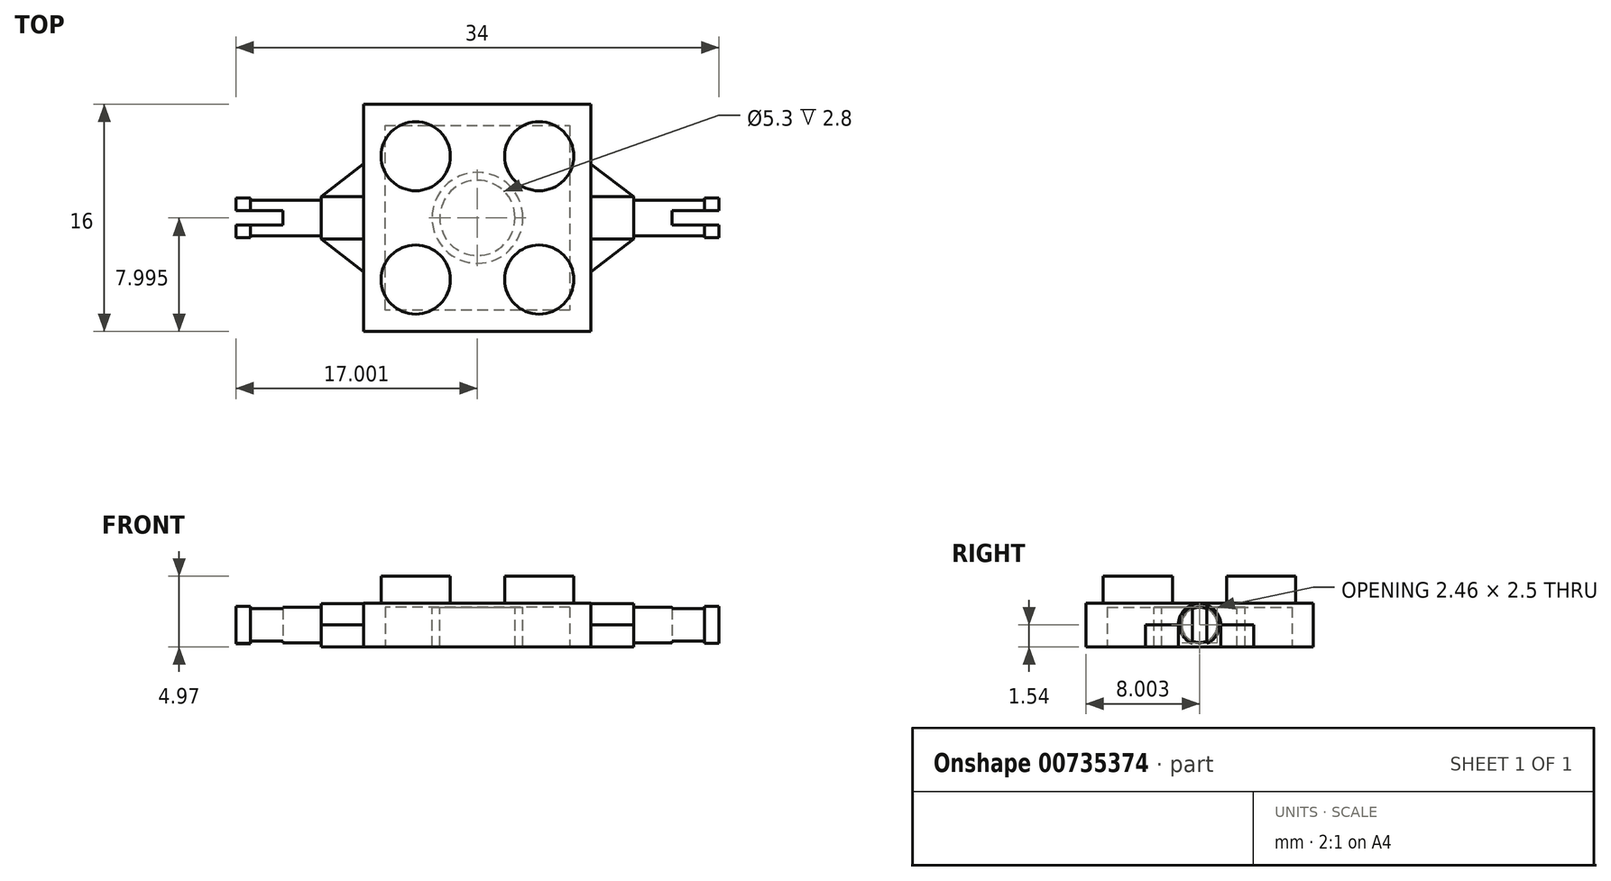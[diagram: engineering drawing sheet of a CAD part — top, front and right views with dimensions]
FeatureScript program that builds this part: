
annotation { "Feature Type Name" : "Feature", "Feature Type Description" : "" }
export const myFeature = defineFeature(function(context is Context, id is Id, definition is map)
    precondition{}
    {
        {
            var Q0;
            Q0=qCreatedBy(makeId("Top.planeOp"),FACE);
            var sketch = newSketch(context, id + "F0", { "sketchPlane" : qUnion([Q0])});
            skLineSegment(sketch, "E0", {"start": v(-18.34, 23.52) * mm, "end": v(-2.34, 23.52) * mm});
            skLineSegment(sketch, "E1", {"start": v(-18.34, 23.52) * mm, "end": v(-18.34, 7.52) * mm});
            skLineSegment(sketch, "E2", {"start": v(-18.34, 7.52) * mm, "end": v(-2.34, 7.52) * mm});
            skLineSegment(sketch, "E3", {"start": v(-2.34, 23.52) * mm, "end": v(-2.34, 7.52) * mm});
            skSolve(sketch);
        }
        {
            var Q0;
            Q0 = qSketchRegion(id + "F0", true);
            extrude(context, id + "F1", {"entities" : qUnion([Q0]), "depth" : 3.08 * mm, "offsetDistance" : 25 * mm});
        }
        {
            var Q0;
            Q0=makeQuery(id+"F1.opExtrude","CAP_FACE",FACE,{"disambiguationData":[OSD([sQuery(id+"F0.wireOp",EDGE,"E0"),sQuery(id+"F0.wireOp",EDGE,"E1"),sQuery(id+"F0.wireOp",EDGE,"E2"),sQuery(id+"F0.wireOp",EDGE,"E3")])],"isStart":false});
            var sketch = newSketch(context, id + "F2", { "sketchPlane" : qUnion([Q0])});
            skCircle(sketch, "E4", {"center": v(-14.68, 19.86) * mm, "radius": 2.44 * mm});
            skCircle(sketch, "E5", {"center": v(-6, 19.86) * mm, "radius": 2.44 * mm});
            skCircle(sketch, "E6", {"center": v(-14.68, 11.17) * mm, "radius": 2.44 * mm});
            skCircle(sketch, "E7", {"center": v(-6, 11.17) * mm, "radius": 2.44 * mm});
            skSolve(sketch);
        }
        {
            var Q0;
            Q0 = qSketchRegion(id + "F2", true);
            extrude(context, id + "F3", {"entities" : qUnion([Q0]), "operationType" : NewBodyOperationType.ADD, "depth" : 1.89 * mm, "offsetDistance" : 25 * mm});
        }
        {
            var Q0;
            Q0=makeQuery(id+"F1.opExtrude","SWEPT_FACE",FACE,{"disambiguationData":[OSD([sQuery(id+"F0.wireOp",EDGE,"E3")])]});
            var sketch = newSketch(context, id + "F4", { "sketchPlane" : qUnion([Q0])});
            skCircle(sketch, "E8", {"center": v(15.52, 1.54) * mm, "radius": 1.5 * mm});
            skPoint(sketch, "E8.centerSnap0", {"position": v(23.52, 1.54) * mm});
            skPoint(sketch, "E8.centerSnap1", {"position": v(15.52, 3.08) * mm});
            skSolve(sketch);
        }
        {
            var Q0;
            Q0 = qSketchRegion(id + "F4", true);
            extrude(context, id + "F5", {"entities" : qUnion([Q0]), "operationType" : NewBodyOperationType.ADD, "depth" : 3 * mm, "offsetDistance" : 25 * mm});
        }
        {
            var Q0;
            Q0=makeQuery(id+"F1.opExtrude","SWEPT_FACE",FACE,{"disambiguationData":[OSD([sQuery(id+"F0.wireOp",EDGE,"E1")])]});
            var sketch = newSketch(context, id + "F6", { "sketchPlane" : qUnion([Q0])});
            skCircle(sketch, "E9", {"center": v(-15.52, 1.54) * mm, "radius": 1.5 * mm});
            skPoint(sketch, "E9.centerSnap0", {"position": v(-7.52, 1.54) * mm});
            skPoint(sketch, "E9.centerSnap1", {"position": v(-15.52, 3.08) * mm});
            skSolve(sketch);
        }
        {
            var Q0;
            Q0 = qSketchRegion(id + "F6", true);
            extrude(context, id + "F7", {"entities" : qUnion([Q0]), "operationType" : NewBodyOperationType.ADD, "depth" : 3 * mm, "offsetDistance" : 25 * mm});
        }
        {
            var Q0;
            Q0=makeQuery(id+"F7.opExtrude","CAP_FACE",FACE,{"disambiguationData":[OSD([sQuery(id+"F6.wireOp",EDGE,"E9")])],"isStart":false});
            var sketch = newSketch(context, id + "F8", { "sketchPlane" : qUnion([Q0])});
            skCircle(sketch, "E10", {"center": v(-15.52, 1.54) * mm, "radius": 1.25 * mm});
            skSolve(sketch);
        }
        {
            var Q0;
            Q0 = qSketchRegion(id + "F8", true);
            extrude(context, id + "F9", {"entities" : qUnion([Q0]), "operationType" : NewBodyOperationType.ADD, "depth" : 5 * mm, "offsetDistance" : 25 * mm});
        }
        {
            var Q0;
            Q0=makeQuery(id+"F5.opExtrude","CAP_FACE",FACE,{"disambiguationData":[OSD([sQuery(id+"F4.wireOp",EDGE,"E8")])],"isStart":false});
            var sketch = newSketch(context, id + "F10", { "sketchPlane" : qUnion([Q0])});
            skCircle(sketch, "E11", {"center": v(15.52, 1.54) * mm, "radius": 1.25 * mm});
            skSolve(sketch);
        }
        {
            var Q0;
            Q0 = qSketchRegion(id + "F10", true);
            extrude(context, id + "F11", {"entities" : qUnion([Q0]), "operationType" : NewBodyOperationType.ADD, "depth" : 5 * mm, "offsetDistance" : 25 * mm});
        }
        {
            var Q0;
            Q0=makeQuery(id+"F1.opExtrude","SWEPT_FACE",FACE,{"disambiguationData":[OSD([sQuery(id+"F0.wireOp",EDGE,"E1")])]});
            var sketch = newSketch(context, id + "F12", { "sketchPlane" : qUnion([Q0])});
            skLineSegment(sketch, "E12", {"start": v(-19.32, 1.54) * mm, "end": v(-19.32, 0) * mm});
            skPoint(sketch, "E12.startSnap0", {"position": v(-23.52, 1.54) * mm});
            skLineSegment(sketch, "E13", {"start": v(-19.32, 0) * mm, "end": v(-11.72, 0) * mm});
            skLineSegment(sketch, "E14", {"start": v(-11.72, 0) * mm, "end": v(-11.72, 1.54) * mm});
            skLineSegment(sketch, "E15", {"start": v(-11.72, 1.54) * mm, "end": v(-14.02, 1.54) * mm});
            skLineSegment(sketch, "E16", {"start": v(-19.32, 1.54) * mm, "end": v(-17.02, 1.54) * mm});
            skSolve(sketch);
        }
        {
            var Q0;
            Q0 = qSketchRegion(id + "F12", true);
            var Q1;
            Q1=makeQuery(id+"F12.imprint","IMPRINT",FACE,{"disambiguationData":[TD([[makeQuery(id+"F12.imprint","IMPRINT",EDGE,{"derivedFrom":sQuery(id+"F12.wireOp",EDGE,"E12")}),1.0]])]});
            extrude(context, id + "F13", {"entities" : qUnion([Q0, Q1]), "operationType" : NewBodyOperationType.ADD, "depth" : 3 * mm, "offsetDistance" : 25 * mm});
        }
        {
            var Q0;
            Q0=makeQuery(id+"F1.opExtrude","SWEPT_FACE",FACE,{"disambiguationData":[OSD([sQuery(id+"F0.wireOp",EDGE,"E3")])]});
            var sketch = newSketch(context, id + "F14", { "sketchPlane" : qUnion([Q0])});
            skLineSegment(sketch, "E17", {"start": v(11.72, 1.54) * mm, "end": v(11.72, 0) * mm});
            skPoint(sketch, "E17.startSnap0", {"position": v(7.52, 1.54) * mm});
            skLineSegment(sketch, "E18", {"start": v(11.72, 0) * mm, "end": v(19.32, 0) * mm});
            skLineSegment(sketch, "E19", {"start": v(19.32, 0) * mm, "end": v(19.32, 1.54) * mm});
            skLineSegment(sketch, "E20", {"start": v(19.32, 1.54) * mm, "end": v(17.02, 1.54) * mm});
            skLineSegment(sketch, "E21", {"start": v(11.72, 1.54) * mm, "end": v(14.02, 1.54) * mm});
            skSolve(sketch);
        }
        {
            var Q0;
            Q0 = qSketchRegion(id + "F14", true);
            var Q1;
            Q1=makeQuery(id+"F14.imprint","IMPRINT",FACE,{"disambiguationData":[TD([[makeQuery(id+"F14.imprint","IMPRINT",EDGE,{"derivedFrom":sQuery(id+"F14.wireOp",EDGE,"E17")}),1.0]])]});
            extrude(context, id + "F15", {"entities" : qUnion([Q0, Q1]), "operationType" : NewBodyOperationType.ADD, "depth" : 3 * mm, "offsetDistance" : 25 * mm});
        }
        {
            var Q0;
            Q0=makeQuery(id+"F13.opExtrude","SWEPT_FACE",FACE,{"disambiguationData":[OSD([sQuery(id+"F12.wireOp",EDGE,"E16")])]});
            var sketch = newSketch(context, id + "F16", { "sketchPlane" : qUnion([Q0])});
            skLineSegment(sketch, "E22", {"start": v(-18.34, 19.32) * mm, "end": v(-21.34, 19.32) * mm});
            skLineSegment(sketch, "E23", {"start": v(-21.34, 19.32) * mm, "end": v(-21.34, 17.02) * mm});
            skLineSegment(sketch, "E24", {"start": v(-21.34, 17.02) * mm, "end": v(-18.34, 19.32) * mm});
            skLineSegment(sketch, "E25", {"start": v(-21.34, 11.72) * mm, "end": v(-21.34, 14.02) * mm});
            skLineSegment(sketch, "E26", {"start": v(-21.34, 14.02) * mm, "end": v(-18.34, 11.72) * mm});
            skLineSegment(sketch, "E27", {"start": v(-18.34, 11.72) * mm, "end": v(-21.34, 11.72) * mm});
            skSolve(sketch);
        }
        {
            var Q0;
            Q0=makeQuery(id+"F16.imprint","IMPRINT",FACE,{"disambiguationData":[TD([[makeQuery(id+"F16.imprint","IMPRINT",EDGE,{"derivedFrom":sQuery(id+"F16.wireOp",EDGE,"E25")}),-1.0]])]});
            var Q1;
            Q1=makeQuery(id+"F16.imprint","IMPRINT",FACE,{"disambiguationData":[TD([[makeQuery(id+"F16.imprint","IMPRINT",EDGE,{"derivedFrom":sQuery(id+"F16.wireOp",EDGE,"E22")}),-1.0]])]});
            extrude(context, id + "F17", {"entities" : qUnion([Q0, Q1]), "operationType" : NewBodyOperationType.REMOVE, "oppositeDirection" : true, "depth" : 25 * mm, "offsetDistance" : 25 * mm});
        }
        {
            var Q0;
            Q0=makeQuery(id+"F15.opExtrude","SWEPT_FACE",FACE,{"disambiguationData":[OSD([sQuery(id+"F14.wireOp",EDGE,"E21")])]});
            var sketch = newSketch(context, id + "F18", { "sketchPlane" : qUnion([Q0])});
            skLineSegment(sketch, "E28", {"start": v(-2.34, 11.72) * mm, "end": v(0.66, 11.72) * mm});
            skLineSegment(sketch, "E29", {"start": v(0.66, 11.72) * mm, "end": v(0.66, 14.02) * mm});
            skLineSegment(sketch, "E30", {"start": v(0.66, 14.02) * mm, "end": v(-2.34, 11.72) * mm});
            skLineSegment(sketch, "E31", {"start": v(-2.34, 19.31) * mm, "end": v(0.66, 17.01) * mm});
            skPoint(sketch, "E32.start.orphan", {"position": v(-2.34, 17.01) * mm});
            skLineSegment(sketch, "E33", {"start": v(-2.34, 19.31) * mm, "end": v(0.66, 19.31) * mm});
            skLineSegment(sketch, "E34", {"start": v(0.66, 19.31) * mm, "end": v(0.66, 17.01) * mm});
            skSolve(sketch);
        }
        {
            var Q0;
            Q0 = qSketchRegion(id + "F18", true);
            extrude(context, id + "F19", {"entities" : qUnion([Q0]), "operationType" : NewBodyOperationType.REMOVE, "oppositeDirection" : true, "depth" : 25 * mm, "offsetDistance" : 25 * mm});
        }
        {
            var Q0;
            Q0=makeQuery(id+"F9.opExtrude","CAP_FACE",FACE,{"disambiguationData":[OSD([sQuery(id+"F8.wireOp",EDGE,"E10")])],"isStart":false});
            var sketch = newSketch(context, id + "F20", { "sketchPlane" : qUnion([Q0])});
            skLineSegment(sketch, "E35", {"start": v(-16.02, 2.69) * mm, "end": v(-16.02, 0.4) * mm});
            skLineSegment(sketch, "E36", {"start": v(-15.02, 2.69) * mm, "end": v(-15.02, 0.4) * mm});
            skSolve(sketch);
        }
        {
            var Q0;
            Q0 = qSketchRegion(id + "F20", true);
            var Q1;
            {var subQ0=sQuery(id+"F20.wireOp",EDGE,"E35");Q1=makeQuery(id+"F20.imprint","IMPRINT",FACE,{"disambiguationData":[TD([[makeQuery(id+"F20.imprint","IMPRINT",EDGE,{"derivedFrom":subQ0}),1.0]])]});}
            extrude(context, id + "F21", {"entities" : qUnion([Q0, Q1]), "operationType" : NewBodyOperationType.REMOVE, "oppositeDirection" : true, "depth" : 2.3 * mm, "offsetDistance" : 25 * mm});
        }
        {
            var Q0;
            Q0=makeQuery(id+"F11.opExtrude","CAP_FACE",FACE,{"disambiguationData":[OSD([sQuery(id+"F10.wireOp",EDGE,"E11")])],"isStart":false});
            var sketch = newSketch(context, id + "F22", { "sketchPlane" : qUnion([Q0])});
            skLineSegment(sketch, "E37", {"start": v(15.02, 2.69) * mm, "end": v(15.02, 0.4) * mm});
            skLineSegment(sketch, "E38", {"start": v(16.02, 2.69) * mm, "end": v(16.02, 0.4) * mm});
            skSolve(sketch);
        }
        {
            var Q0;
            Q0 = qSketchRegion(id + "F22", true);
            var Q1;
            {var subQ0=sQuery(id+"F22.wireOp",EDGE,"E37");Q1=makeQuery(id+"F22.imprint","IMPRINT",FACE,{"disambiguationData":[TD([[makeQuery(id+"F22.imprint","IMPRINT",EDGE,{"derivedFrom":subQ0}),1.0]])]});}
            extrude(context, id + "F23", {"entities" : qUnion([Q0, Q1]), "operationType" : NewBodyOperationType.REMOVE, "oppositeDirection" : true, "depth" : 2.3 * mm, "offsetDistance" : 25 * mm});
        }
        {
            var Q0;
            {var subQ0=sQuery(id+"F8.wireOp",EDGE,"E10");Q0=makeQuery(id+"F21.boolean.opBoolean","SPLIT",FACE,{"disambiguationData":[TD([makeQuery(id+"F21.opExtrude","SWEPT_FACE",FACE,{"disambiguationData":[OSD([sQuery(id+"F20.wireOp",EDGE,"E36")])]})])],"derivedFrom":makeQuery(id+"F9.opExtrude","CAP_FACE",FACE,{"disambiguationData":[OSD([subQ0])],"isStart":false})});}
            var sketch = newSketch(context, id + "F24", { "sketchPlane" : qUnion([Q0])});
            skCircle(sketch, "E39", {"center": v(-15.52, 1.54) * mm, "radius": 1.4 * mm});
            skLineSegment(sketch, "E40", {"start": v(-16.02, 2.85) * mm, "end": v(-16.02, 0.23) * mm});
            skLineSegment(sketch, "E41", {"start": v(-15.02, 2.85) * mm, "end": v(-15.02, 0.23) * mm});
            skSolve(sketch);
        }
        {
            var Q0;
            {var subQ4=sQuery(id+"F8.wireOp",EDGE,"E10");var subQ5=makeQuery(id+"F21.boolean.opBoolean","SPLIT",EDGE,{"disambiguationData":[TD([makeQuery(id+"F21.opExtrude","SWEPT_FACE",FACE,{"disambiguationData":[OSD([sQuery(id+"F20.wireOp",EDGE,"E36")])]})])],"derivedFrom":makeQuery(id+"F9.opExtrude","CAP_EDGE",EDGE,{"disambiguationData":[OSD([subQ4])],"isStart":false})});Q0=makeQuery(id+"F24.imprint","IMPRINT",FACE,{"disambiguationData":[TD([[makeQuery(id+"F24.imprint","IMPRINT",EDGE,{"derivedFrom":subQ5}),-1.0]])]});}
            var Q1;
            {var subQ0=sQuery(id+"F24.wireOp",EDGE,"E40");Q1=makeQuery(id+"F24.imprint","IMPRINT",FACE,{"disambiguationData":[TD([[makeQuery(id+"F24.imprint","IMPRINT",EDGE,{"derivedFrom":subQ0}),-1.0]])]});}
            var Q2;
            {var subQ1=sQuery(id+"F8.wireOp",EDGE,"E10");var subQ2=makeQuery(id+"F21.boolean.opBoolean","SPLIT",EDGE,{"disambiguationData":[TD([makeQuery(id+"F21.opExtrude","SWEPT_FACE",FACE,{"disambiguationData":[OSD([sQuery(id+"F20.wireOp",EDGE,"E36")])]})])],"derivedFrom":makeQuery(id+"F9.opExtrude","CAP_EDGE",EDGE,{"disambiguationData":[OSD([subQ1])],"isStart":false})});Q2=makeQuery(id+"F24.imprint","IMPRINT",FACE,{"disambiguationData":[TD([[makeQuery(id+"F24.imprint","IMPRINT",EDGE,{"derivedFrom":subQ2}),1.0]])]});}
            extrude(context, id + "F25", {"entities" : qUnion([Q0, Q1, Q2]), "operationType" : NewBodyOperationType.ADD, "depth" : 1 * mm, "offsetDistance" : 25 * mm});
        }
        {
            var Q0;
            {var subQ0=sQuery(id+"F10.wireOp",EDGE,"E11");Q0=makeQuery(id+"F23.boolean.opBoolean","SPLIT",FACE,{"disambiguationData":[TD([makeQuery(id+"F23.opExtrude","SWEPT_FACE",FACE,{"disambiguationData":[OSD([sQuery(id+"F22.wireOp",EDGE,"E37")])]})])],"derivedFrom":makeQuery(id+"F11.opExtrude","CAP_FACE",FACE,{"disambiguationData":[OSD([subQ0])],"isStart":false})});}
            var sketch = newSketch(context, id + "F26", { "sketchPlane" : qUnion([Q0])});
            skArc(sketch, "E42", {"start": v(15.02, 2.85) * mm, "mid": v(14.12, 1.54) * mm, "end": v(15.02, 0.23) * mm});
            skLineSegment(sketch, "E43", {"start": v(15.02, 2.85) * mm, "end": v(15.02, 0.23) * mm});
            skLineSegment(sketch, "E44", {"start": v(16.02, 2.85) * mm, "end": v(16.02, 0.23) * mm});
            skArc(sketch, "E45.trimOffspring", {"start": v(16.02, 0.23) * mm, "mid": v(16.92, 1.54) * mm, "end": v(16.02, 2.85) * mm});
            skSolve(sketch);
        }
        {
            var Q0;
            Q0 = qSketchRegion(id + "F26", true);
            var Q1;
            Q1 = qSketchRegion(id + "F28", true);
            extrude(context, id + "F27", {"entities" : qUnion([Q0, Q1]), "operationType" : NewBodyOperationType.ADD, "depth" : 1 * mm, "offsetDistance" : 25 * mm});
        }
        {
            var Q0;
            Q0=makeQuery(id+"F15.boolean.opBoolean","MERGE",FACE,{"derivedFrom":[makeQuery(id+"F13.boolean.opBoolean","MERGE",FACE,{"derivedFrom":[makeQuery(id+"F1.opExtrude","CAP_FACE",FACE,{"disambiguationData":[OSD([sQuery(id+"F0.wireOp",EDGE,"E0"),sQuery(id+"F0.wireOp",EDGE,"E1"),sQuery(id+"F0.wireOp",EDGE,"E2"),sQuery(id+"F0.wireOp",EDGE,"E3")])],"isStart":true}),makeQuery(id+"F13.opExtrude","SWEPT_FACE",FACE,{"disambiguationData":[OSD([sQuery(id+"F12.wireOp",EDGE,"E13")])]})]}),makeQuery(id+"F15.opExtrude","SWEPT_FACE",FACE,{"disambiguationData":[OSD([sQuery(id+"F14.wireOp",EDGE,"E18")])]})]});
            var sketch = newSketch(context, id + "F28", { "sketchPlane" : qUnion([Q0])});
            skLineSegment(sketch, "E46", {"start": v(-16.84, -9.02) * mm, "end": v(-16.84, -22.02) * mm});
            skLineSegment(sketch, "E47", {"start": v(-16.84, -22.02) * mm, "end": v(-3.84, -22.02) * mm});
            skLineSegment(sketch, "E48", {"start": v(-3.84, -22.02) * mm, "end": v(-3.84, -9.02) * mm});
            skLineSegment(sketch, "E49", {"start": v(-3.84, -9.02) * mm, "end": v(-16.84, -9.02) * mm});
            skSolve(sketch);
        }
        {
            var Q0;
            Q0 = qSketchRegion(id + "F28", true);
            extrude(context, id + "F29", {"entities" : qUnion([Q0]), "operationType" : NewBodyOperationType.REMOVE, "oppositeDirection" : true, "depth" : 2.8 * mm, "offsetDistance" : 25 * mm});
        }
        {
            var Q0;
            Q0=makeQuery(id+"F29.boolean.opBoolean","COPY",FACE,{"derivedFrom":makeQuery(id+"F29.opExtrude","CAP_FACE",FACE,{"disambiguationData":[OSD([sQuery(id+"F28.wireOp",EDGE,"E46"),sQuery(id+"F28.wireOp",EDGE,"E47"),sQuery(id+"F28.wireOp",EDGE,"E48"),sQuery(id+"F28.wireOp",EDGE,"E49")])],"isStart":false})});
            var sketch = newSketch(context, id + "F30", { "sketchPlane" : qUnion([Q0])});
            skCircle(sketch, "E50", {"center": v(-10.34, -15.52) * mm, "radius": 3.2 * mm});
            skPoint(sketch, "E51.start.orphan", {"position": v(-16.84, -15.52) * mm});
            skPoint(sketch, "E52.trimOffspring.end.orphan", {"position": v(-3.84, -15.52) * mm});
            skCircle(sketch, "E53", {"center": v(-10.34, -15.52) * mm, "radius": 2.65 * mm});
            skSolve(sketch);
        }
        {
            var Q0;
            Q0 = qSketchRegion(id + "F30", true);
            extrude(context, id + "F31", {"entities" : qUnion([Q0]), "operationType" : NewBodyOperationType.ADD, "depth" : 2.8 * mm, "offsetDistance" : 25 * mm});
        }
    });
